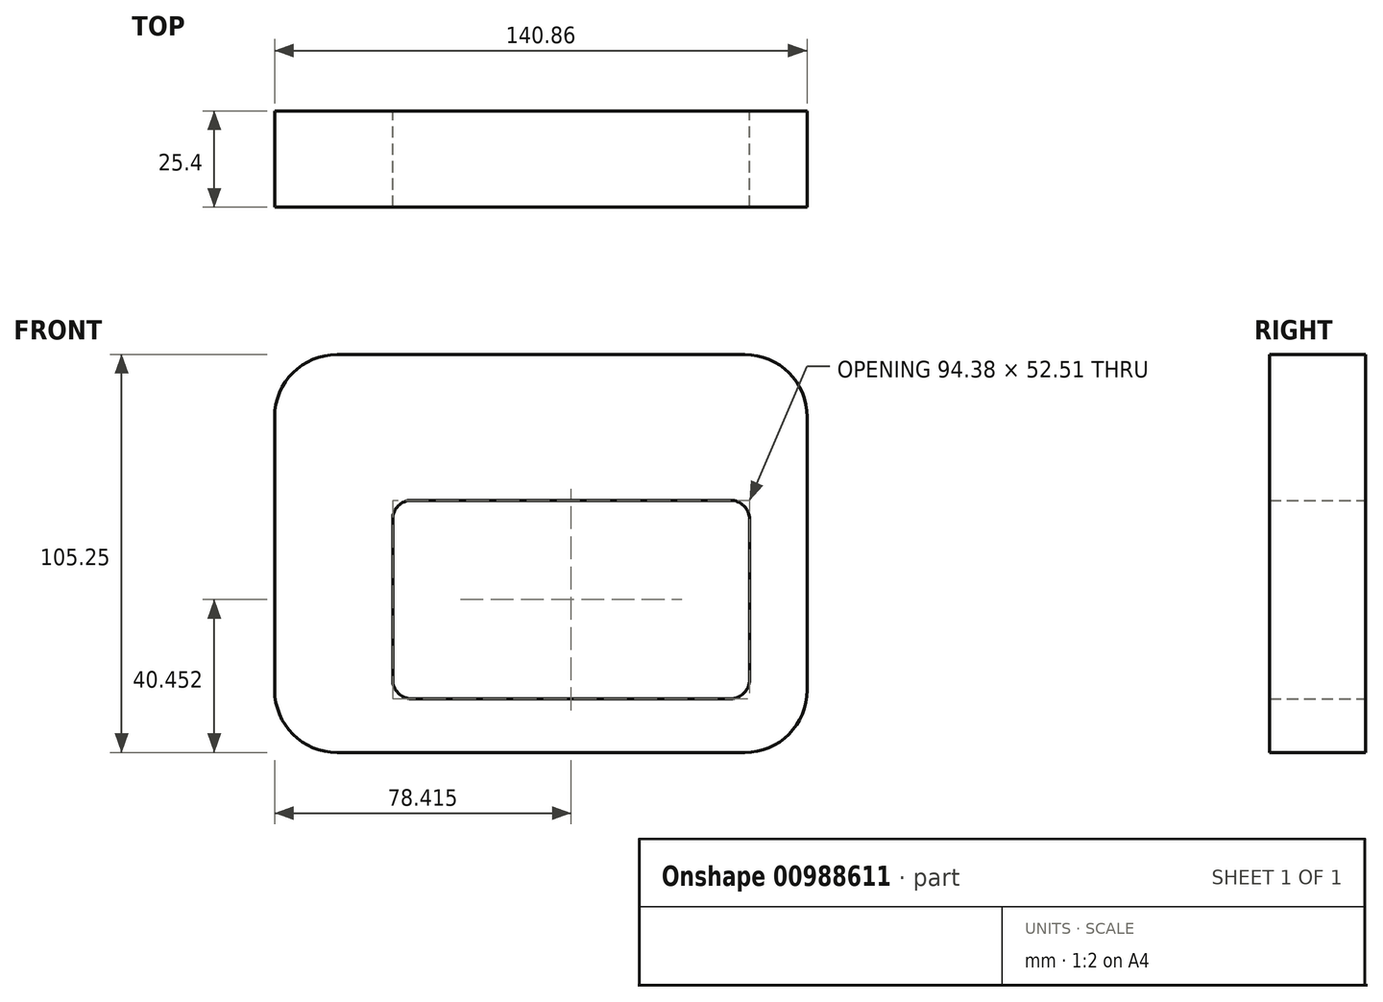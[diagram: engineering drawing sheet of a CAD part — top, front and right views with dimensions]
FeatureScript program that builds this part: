
annotation { "Feature Type Name" : "Feature", "Feature Type Description" : "" }
export const myFeature = defineFeature(function(context is Context, id is Id, definition is map)
    precondition{}
    {
        {
            var Q0;
            Q0=qCreatedBy(makeId("Front.planeOp"),FACE);
            var sketch = newSketch(context, id + "F0", { "sketchPlane" : qUnion([Q0])});
            skLineSegment(sketch, "E0.bottom", {"start": v(-50.35, 56.58) * mm, "end": v(57.5, 56.58) * mm});
            skLineSegment(sketch, "E0.top", {"start": v(-50.35, -48.67) * mm, "end": v(57.5, -48.67) * mm});
            skLineSegment(sketch, "E0.left", {"start": v(-66.86, 40.07) * mm, "end": v(-66.86, -32.16) * mm});
            skLineSegment(sketch, "E0.right", {"start": v(74, 40.07) * mm, "end": v(74, -32.16) * mm});
            skLineSegment(sketch, "E1.bottom", {"start": v(-35.63, 18.04) * mm, "end": v(58.74, 18.04) * mm});
            skLineSegment(sketch, "E1.top", {"start": v(-35.63, -34.47) * mm, "end": v(58.74, -34.47) * mm});
            skLineSegment(sketch, "E1.left", {"start": v(-35.63, 18.04) * mm, "end": v(-35.63, -34.47) * mm});
            skLineSegment(sketch, "E1.right", {"start": v(58.74, 18.04) * mm, "end": v(58.74, -34.47) * mm});
            skPoint(sketch, "E2.visualSharp", {"position": v(-66.86, 56.58) * mm});
            skArc(sketch, "E2.filletArc", {"start": v(-50.35, 56.58) * mm, "mid": v(-62.02, 51.75) * mm, "end": v(-66.86, 40.07) * mm});
            skPoint(sketch, "E3.visualSharp", {"position": v(74, 56.58) * mm});
            skArc(sketch, "E3.filletArc", {"start": v(74, 40.07) * mm, "mid": v(69.17, 51.75) * mm, "end": v(57.5, 56.58) * mm});
            skPoint(sketch, "E4.visualSharp", {"position": v(74, -48.67) * mm});
            skArc(sketch, "E4.filletArc", {"start": v(57.5, -48.67) * mm, "mid": v(69.17, -43.83) * mm, "end": v(74, -32.16) * mm});
            skPoint(sketch, "E5.visualSharp", {"position": v(-66.86, -48.67) * mm});
            skArc(sketch, "E5.filletArc", {"start": v(-66.86, -32.16) * mm, "mid": v(-62.02, -43.83) * mm, "end": v(-50.35, -48.67) * mm});
            skSolve(sketch);
        }
        {
            var Q0;
            Q0 = qSketchRegion(id + "F0", true);
            extrude(context, id + "F1", {"entities" : qUnion([Q0]), "depth" : 25.4 * mm, "offsetDistance" : 25.4 * mm});
        }
        {
            var Q0;
            Q0=makeQuery(id+"F1.opExtrude","SWEPT_EDGE",EDGE,{"disambiguationData":[OSD([sQuery(id+"F0.wireOp",EDGE,"E1.bottom"),sQuery(id+"F0.wireOp",EDGE,"E1.left")])]});
            var Q1;
            Q1=makeQuery(id+"F1.opExtrude","SWEPT_EDGE",EDGE,{"disambiguationData":[OSD([sQuery(id+"F0.wireOp",EDGE,"E1.bottom"),sQuery(id+"F0.wireOp",EDGE,"E1.right")])]});
            var Q2;
            Q2=makeQuery(id+"F1.opExtrude","SWEPT_EDGE",EDGE,{"disambiguationData":[OSD([sQuery(id+"F0.wireOp",EDGE,"E1.top"),sQuery(id+"F0.wireOp",EDGE,"E1.right")])]});
            var Q3;
            Q3=makeQuery(id+"F1.opExtrude","SWEPT_EDGE",EDGE,{"disambiguationData":[OSD([sQuery(id+"F0.wireOp",EDGE,"E1.top"),sQuery(id+"F0.wireOp",EDGE,"E1.left")])]});
            fillet(context, id + "F2", {"entities" : qUnion([Q0, Q1, Q2, Q3]), "radius" : 5.08 * mm, "tangentPropagation" : true, "allowEdgeOverflow" : false});
        }
    });
